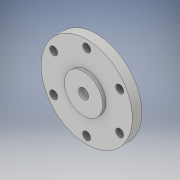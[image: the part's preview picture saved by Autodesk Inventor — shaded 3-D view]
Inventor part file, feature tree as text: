
AUTODESK INVENTOR PART (.ipt)
format: ipt  version: 2017 (Build 210142000, 142)  size: 130,560 bytes
history: native  units: in
note: dims shown in document units (in); Inventor stores cm internally (conversion verified against a paired STEP export)
features: sketch x4, extrude x3, hole x1, pattern_circular x1, projected_geometry x1
ambient origin geometry x8: Origin, YZ Plane, XZ Plane, XY Plane, X Axis, Y Axis, Z Axis, Center Point
bodies: Solid1 (feature_tree)
feature tree (10):
  extrude  "Extrusion1"  Depth=0.236in TaperAngle=0.0deg
  extrude  "Extrusion2"  Depth=0.075in TaperAngle=0.0deg
  extrude  "Extrusion3"  Depth=1.0in TaperAngle=0.0deg
  hole  "Hole1"  [1 undecoded]
  pattern_circular  "Circular Pattern1"  [2 undecoded]
  sketch  "Sketch1"  dims[d0=2.236in d1=0.236in d2=0.0in]
  sketch  "Sketch2"  dims[d3=0.944in d4=0.075in d5=0.0in]
  sketch  "Sketch3"  dims[d6=0.25in d7=1.0in d8=0.0in]
  sketch  "Sketch4"  dims[d10=0.196in d11=0.5in d12=0.375in d13=0.25in d14=0.5635in d15=0.75in d16=0.8108in d17=2.3622in d18=360.0deg]
  projected_geometry  "Projected Loop1"
note: 3 required parameter values undecoded (feature->parameter linkage not recoverable at this tier; creation-order binding heuristic only, values carry confidence <= 0.55)
